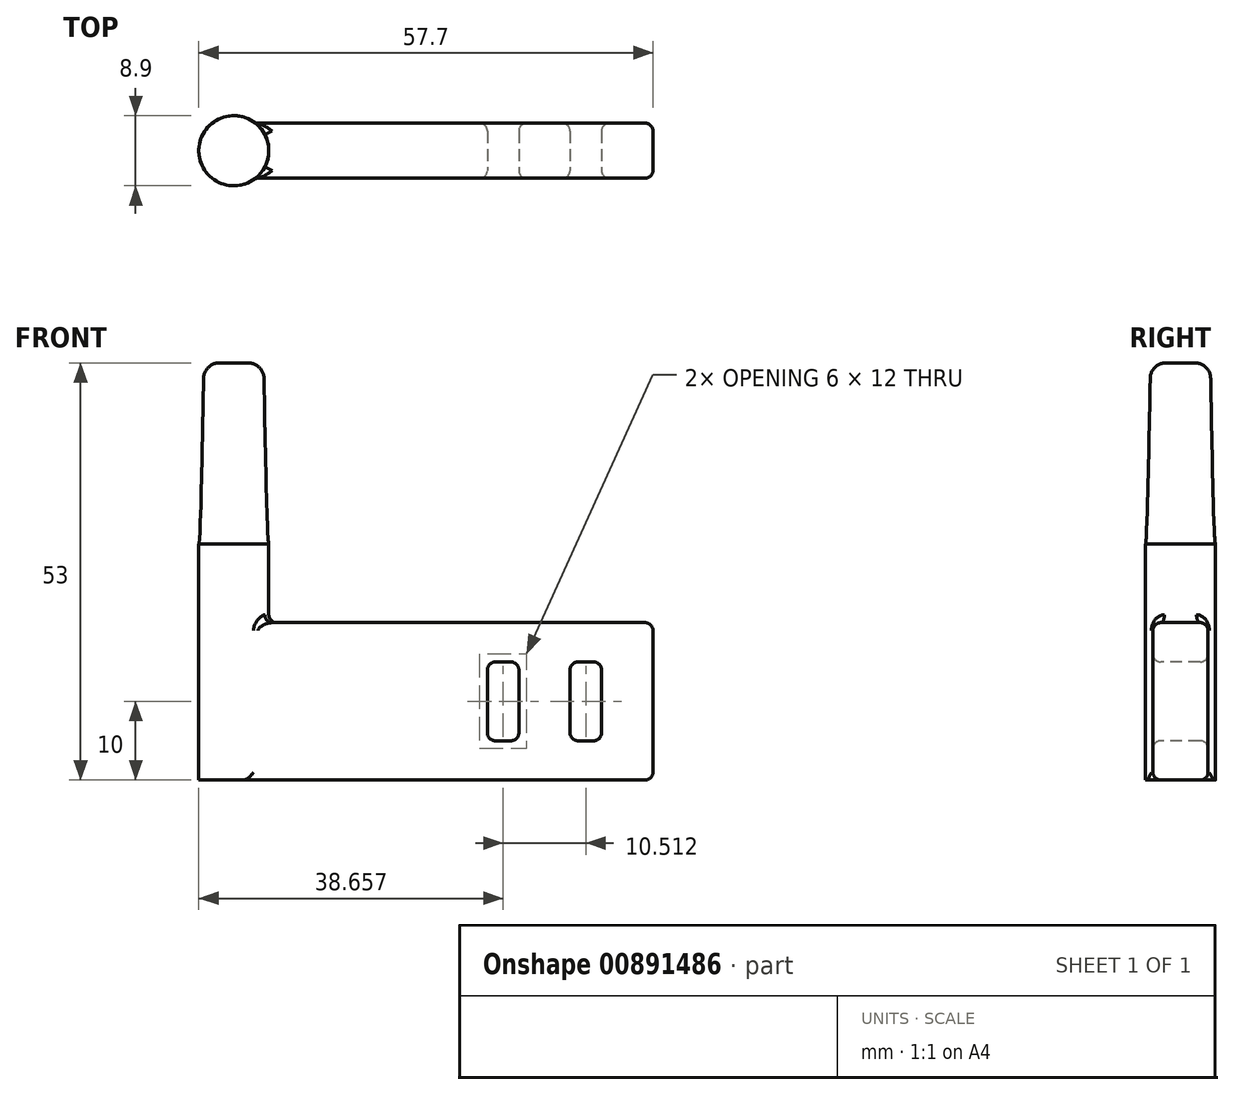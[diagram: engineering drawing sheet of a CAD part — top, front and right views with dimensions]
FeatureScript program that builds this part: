
annotation { "Feature Type Name" : "Feature", "Feature Type Description" : "" }
export const myFeature = defineFeature(function(context is Context, id is Id, definition is map)
    precondition{}
    {
        {
            var Q0;
            Q0=qCreatedBy(makeId("Top.planeOp"),FACE);
            var sketch = newSketch(context, id + "F0", { "sketchPlane" : qUnion([Q0])});
            skCircle(sketch, "E0", {"center": v(0, 0) * mm, "radius": 4.45 * mm});
            skLineSegment(sketch, "E1.bottom", {"start": v(2.75, 3.5) * mm, "end": v(53.25, 3.5) * mm});
            skLineSegment(sketch, "E1.top", {"start": v(2.75, -3.5) * mm, "end": v(53.25, -3.5) * mm});
            skLineSegment(sketch, "E1.right", {"start": v(53.25, 3.5) * mm, "end": v(53.25, -3.5) * mm});
            skSolve(sketch);
        }
        {
            var Q0;
            {var subQ0=sQuery(id+"F0.wireOp",EDGE,"E1.bottom");Q0=makeQuery(id+"F0.imprint","IMPRINT",FACE,{"disambiguationData":[TD([[makeQuery(id+"F0.imprint","IMPRINT",EDGE,{"derivedFrom":subQ0}),-1.0]])]});}
            extrude(context, id + "F1", {"entities" : qUnion([Q0]), "depth" : 20 * mm, "offsetDistance" : 25 * mm});
        }
        {
            var Q0;
            {var subQ0=sQuery(id+"F0.wireOp",EDGE,"E0");var subQ1=makeQuery(id+"F0.imprint","INTERSECT",VERTEX,{"derivedFrom":[subQ0,sQuery(id+"F0.wireOp",EDGE,"E1.bottom")]});Q0=makeQuery(id+"F0.imprint","IMPRINT",FACE,{"disambiguationData":[TD([[makeQuery(id+"F0.imprint","IMPRINT",EDGE,{"disambiguationData":[TD([[subQ1,-1.0]])],"derivedFrom":subQ0}),1.0]])]});}
            extrude(context, id + "F2", {"entities" : qUnion([Q0]), "operationType" : NewBodyOperationType.ADD, "depth" : 30 * mm, "offsetDistance" : 25 * mm});
        }
        {
            var Q0;
            Q0=makeQuery(id+"F2.opExtrude","CAP_FACE",FACE,{"disambiguationData":[OSD([sQuery(id+"F0.wireOp",EDGE,"E0")])],"isStart":false});
            var sketch = newSketch(context, id + "F3", { "sketchPlane" : qUnion([Q0])});
            skSolve(sketch);
        }
        {
            var Q0;
            Q0=makeQuery(id+"F3.imprint","IMPRINT",FACE,{"disambiguationData":[TD([[makeQuery(id+"F3.imprint","IMPRINT",EDGE,{"derivedFrom":makeQuery(id+"F2.opExtrude","CAP_EDGE",EDGE,{"disambiguationData":[OSD([sQuery(id+"F0.wireOp",EDGE,"E0")])],"isStart":false})}),1.0]])]});
            cPlane(context, id + "F4", {"entities" : qUnion([Q0]), "cplaneType" : CPlaneType.OFFSET, "offset" : 23 * mm, "width" : 150 * mm, "height" : 150 * mm});
        }
        {
            var Q0;
            Q0=qCreatedBy(id+"F4.planeOp",FACE);
            var sketch = newSketch(context, id + "F5", { "sketchPlane" : qUnion([Q0])});
            skPoint(sketch, "E2.0", {"position": v(0, 0) * mm});
            skCircle(sketch, "E3", {"center": v(0, 0) * mm, "radius": 3.8 * mm});
            skSolve(sketch);
        }
        {
            var Q0;
            Q0=makeQuery(id+"F3.imprint","IMPRINT",FACE,{"disambiguationData":[TD([[makeQuery(id+"F3.imprint","IMPRINT",EDGE,{"derivedFrom":makeQuery(id+"F2.opExtrude","CAP_EDGE",EDGE,{"disambiguationData":[OSD([sQuery(id+"F0.wireOp",EDGE,"E0")])],"isStart":false})}),1.0]])]});
            var Q1;
            Q1=makeQuery(id+"F5.imprint","IMPRINT",FACE,{"disambiguationData":[TD([[makeQuery(id+"F5.imprint","IMPRINT",EDGE,{"derivedFrom":sQuery(id+"F5.wireOp",EDGE,"E3")}),1.0]])]});
            loft(context, id + "F6", {"startCondition" : LoftEndDerivativeType.TANGENT_TO_PROFILE, "startMagnitude" : 1, "sheetProfilesArray" : [{ "sheetProfileEntities" : qUnion([Q0]) }, { "sheetProfileEntities" : qUnion([Q1]) }]});
        }
        {
            var Q0;
            Q0=makeQuery(id+"F6.opLoft","MID_CAP_EDGE",EDGE,{"disambiguationData":[OSD([sQuery(id+"F5.wireOp",EDGE,"E3")])],"capPos":1.0});
            fillet(context, id + "F7", {"entities" : qUnion([Q0]), "radius" : 2 * mm, "tangentPropagation" : true, "allowEdgeOverflow" : false});
        }
        {
            var Q0;
            Q0=makeQuery(id+"F1.opExtrude","SWEPT_FACE",FACE,{"disambiguationData":[OSD([sQuery(id+"F0.wireOp",EDGE,"E1.top")])]});
            var sketch = newSketch(context, id + "F8", { "sketchPlane" : qUnion([Q0])});
            skLineSegment(sketch, "E4.bottom", {"start": v(43.72, 5) * mm, "end": v(45.72, 5) * mm});
            skLineSegment(sketch, "E4.top", {"start": v(43.72, 15) * mm, "end": v(45.72, 15) * mm});
            skLineSegment(sketch, "E4.left", {"start": v(42.72, 6) * mm, "end": v(42.72, 14) * mm});
            skLineSegment(sketch, "E4.right", {"start": v(46.72, 6) * mm, "end": v(46.72, 14) * mm});
            skPoint(sketch, "E4.middle", {"position": v(44.72, 10) * mm});
            skPoint(sketch, "E4.middle.positionSnap0", {"position": v(53.25, 10) * mm});
            skPoint(sketch, "E4.centerSnap0", {"position": v(53.25, 10) * mm});
            skLineSegment(sketch, "E5", {"start": v(39.46, 17.47) * mm, "end": v(39.46, 1.7) * mm, "construction": true});
            skLineSegment(sketch, "E6.MirrorCS", {"start": v(36.2, 6) * mm, "end": v(36.2, 14) * mm});
            skLineSegment(sketch, "E7.MirrorCS", {"start": v(35.2, 15) * mm, "end": v(33.2, 15) * mm});
            skLineSegment(sketch, "E8.MirrorCS", {"start": v(32.2, 6) * mm, "end": v(32.2, 14) * mm});
            skLineSegment(sketch, "E9.MirrorCS", {"start": v(35.2, 5) * mm, "end": v(33.2, 5) * mm});
            skPoint(sketch, "E10.visualSharp", {"position": v(41.77, 12.61) * mm});
            skPoint(sketch, "E11.visualSharp", {"position": v(42.72, 15) * mm});
            skArc(sketch, "E11.filletArc", {"start": v(43.72, 15) * mm, "mid": v(43.01, 14.7) * mm, "end": v(42.72, 14) * mm});
            skPoint(sketch, "E12.visualSharp", {"position": v(46.72, 15) * mm});
            skArc(sketch, "E12.filletArc", {"start": v(46.72, 14) * mm, "mid": v(46.43, 14.7) * mm, "end": v(45.72, 15) * mm});
            skPoint(sketch, "E13.visualSharp", {"position": v(42.72, 5) * mm});
            skArc(sketch, "E13.filletArc", {"start": v(42.72, 6) * mm, "mid": v(43.01, 5.3) * mm, "end": v(43.72, 5) * mm});
            skPoint(sketch, "E14.visualSharp", {"position": v(46.72, 5) * mm});
            skArc(sketch, "E14.filletArc", {"start": v(45.72, 5) * mm, "mid": v(46.43, 5.3) * mm, "end": v(46.72, 6) * mm});
            skPoint(sketch, "E15.visualSharp", {"position": v(32.2, 5) * mm});
            skArc(sketch, "E15.filletArc", {"start": v(32.2, 6) * mm, "mid": v(32.5, 5.3) * mm, "end": v(33.2, 5) * mm});
            skPoint(sketch, "E16.visualSharp", {"position": v(32.2, 15) * mm});
            skArc(sketch, "E16.filletArc", {"start": v(33.2, 15) * mm, "mid": v(32.5, 14.7) * mm, "end": v(32.2, 14) * mm});
            skPoint(sketch, "E17.visualSharp", {"position": v(36.2, 15) * mm});
            skArc(sketch, "E17.filletArc", {"start": v(36.2, 14) * mm, "mid": v(35.91, 14.7) * mm, "end": v(35.2, 15) * mm});
            skPoint(sketch, "E18.visualSharp", {"position": v(36.2, 5) * mm});
            skArc(sketch, "E18.filletArc", {"start": v(35.2, 5) * mm, "mid": v(35.91, 5.3) * mm, "end": v(36.2, 6) * mm});
            skSolve(sketch);
        }
        {
            var Q0;
            Q0=makeQuery(id+"F8.imprint","IMPRINT",FACE,{"disambiguationData":[TD([[makeQuery(id+"F8.imprint","IMPRINT",EDGE,{"derivedFrom":sQuery(id+"F8.wireOp",EDGE,"E4.bottom")}),1.0]])]});
            var Q1;
            Q1=makeQuery(id+"F8.imprint","IMPRINT",FACE,{"disambiguationData":[TD([[makeQuery(id+"F8.imprint","IMPRINT",EDGE,{"derivedFrom":sQuery(id+"F8.wireOp",EDGE,"E6.MirrorCS")}),1.0]])]});
            var Q2;
            Q2=makeQuery(id+"F1.opExtrude","SWEPT_FACE",FACE,{"disambiguationData":[OSD([sQuery(id+"F0.wireOp",EDGE,"E1.bottom")])]});
            extrude(context, id + "F9", {"entities" : qUnion([Q0, Q1]), "operationType" : NewBodyOperationType.REMOVE, "endBound" : BoundingType.UP_TO_SURFACE, "oppositeDirection" : true, "depth" : 25 * mm, "endBoundEntityFace" : qUnion([Q2]), "offsetDistance" : 25 * mm});
        }
        {
            var Q0;
            Q0=makeQuery(id+"F1.opExtrude","CAP_EDGE",EDGE,{"disambiguationData":[OSD([sQuery(id+"F0.wireOp",EDGE,"E1.top")])],"isStart":false});
            var Q1;
            Q1=makeQuery(id+"F1.opExtrude","CAP_EDGE",EDGE,{"disambiguationData":[OSD([sQuery(id+"F0.wireOp",EDGE,"E1.top")])],"isStart":true});
            var Q2;
            Q2=makeQuery(id+"F1.opExtrude","SWEPT_EDGE",EDGE,{"disambiguationData":[OSD([sQuery(id+"F0.wireOp",EDGE,"E1.top"),sQuery(id+"F0.wireOp",EDGE,"E1.right")])]});
            var Q3;
            Q3=makeQuery(id+"F1.opExtrude","SWEPT_FACE",FACE,{"disambiguationData":[OSD([sQuery(id+"F0.wireOp",EDGE,"E1.bottom")])]});
            var Q4;
            Q4=makeQuery(id+"F1.opExtrude","CAP_FACE",FACE,{"disambiguationData":[OSD([sQuery(id+"F0.wireOp",EDGE,"E0"),sQuery(id+"F0.wireOp",EDGE,"E1.bottom"),sQuery(id+"F0.wireOp",EDGE,"E1.top"),sQuery(id+"F0.wireOp",EDGE,"E1.right")])],"isStart":false});
            var Q5;
            Q5=makeQuery(id+"F1.opExtrude","SWEPT_FACE",FACE,{"disambiguationData":[OSD([sQuery(id+"F0.wireOp",EDGE,"E1.right")])]});
            var Q6;
            Q6=makeQuery(id+"F1.opExtrude","SWEPT_FACE",FACE,{"disambiguationData":[OSD([sQuery(id+"F0.wireOp",EDGE,"E1.top")])]});
            fillet(context, id + "F10", {"entities" : qUnion([Q0, Q1, Q2, Q3, Q4, Q5, Q6]), "radius" : 1 * mm, "tangentPropagation" : true, "allowEdgeOverflow" : false});
        }
    });
